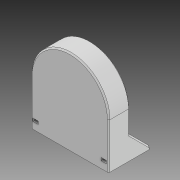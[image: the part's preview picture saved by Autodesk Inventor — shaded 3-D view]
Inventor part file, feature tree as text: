
AUTODESK INVENTOR PART (.ipt)
format: ipt  version: 2020 (Build 240168000, 168)  size: 387,072 bytes
history: native  units: mm
features: extrude x10, sketch x9, fillet x2, chamfer x2, projected_geometry x2, mirror x1, plane x1
ambient origin geometry x8: Origin, YZ Plane, XZ Plane, XY Plane, X Axis, Y Axis, Z Axis, Center Point
bodies: Solid1 (feature_tree)
feature tree (27):
  extrude  "Extrusion1"  Depth=70.0mm
  extrude  "Extrusion2"  Depth=32.5mm
  extrude  "Extrusion3"  Depth=1.0mm
  extrude  "Extrusion7"  Depth=50.0mm TaperAngle=360.0deg
  mirror  "Mirror1"
  extrude  "Extrusion4"  Depth=5.5mm
  plane  "Work Plane1"
  sketch  "Sketch6"  dims[d14=0.0mm d15=0.0mm d16=5.5mm]
  extrude  "Extrusion5"  Depth=7.5mm
  extrude  "Extrusion6"  [1 undecoded]
  fillet  "Fillet1"  Radius=8.2mm
  chamfer  "Chamfer1"  Distance=4.5mm
  fillet  "Fillet2"  Radius=20.75mm
  chamfer  "Chamfer2"  Distance=2.0mm Angle=45.0deg
  extrude  "Extrusion8"  Depth=5.0mm
  extrude  "Extrusion9"  TaperAngle=135.0deg  [1 undecoded]
  extrude  "Extrusion10"  Depth=15.0mm TaperAngle=0.0deg
  sketch  "Sketch1"  dims[d0=95.05mm d2=70.0mm]
  sketch  "Sketch2"  dims[d3=32.5mm d4=0.0mm d5=2.0mm]
  sketch  "Sketch3"  dims[d6=1.0mm d7=0.0mm d8=5.2mm]
  sketch  "Sketch5"  dims[d9=55.0mm d10=50.0mm d12=360.0deg]
  sketch  "Sketch7"  dims[d17=7.5mm d18=7.5mm]
  projected_geometry  "Projected Loop2"
  sketch  "Sketch9"  dims[d20=18.0mm d21=0.0mm d22=-15.0mm d23=8.2mm d24=4.5mm d25=0.0mm d26=20.75mm d27=0.0mm]
  projected_geometry  "Projected Loop4"
  sketch  "Sketch10"  dims[d28=2.0mm d29=2.0mm d30=2.0mm d31=45.0deg]
  sketch  "Sketch11"  dims[d32=30.0mm d33=5.0mm d34=135.0deg d35=15.0mm d36=0.0mm d37=10.0mm d38=5.0mm d39=17.5mm d40=2.0mm d41=2.0mm d42=45.0deg d43=60.0mm d45=52.5mm d46=45.0mm d47=7.5mm d48=0.0mm d49=0.0mm d50=1.0mm d51=0.0mm d52=3.0mm d53=0.0mm]
note: 2 required parameter values undecoded (feature->parameter linkage not recoverable at this tier; creation-order binding heuristic only, values carry confidence <= 0.55)
